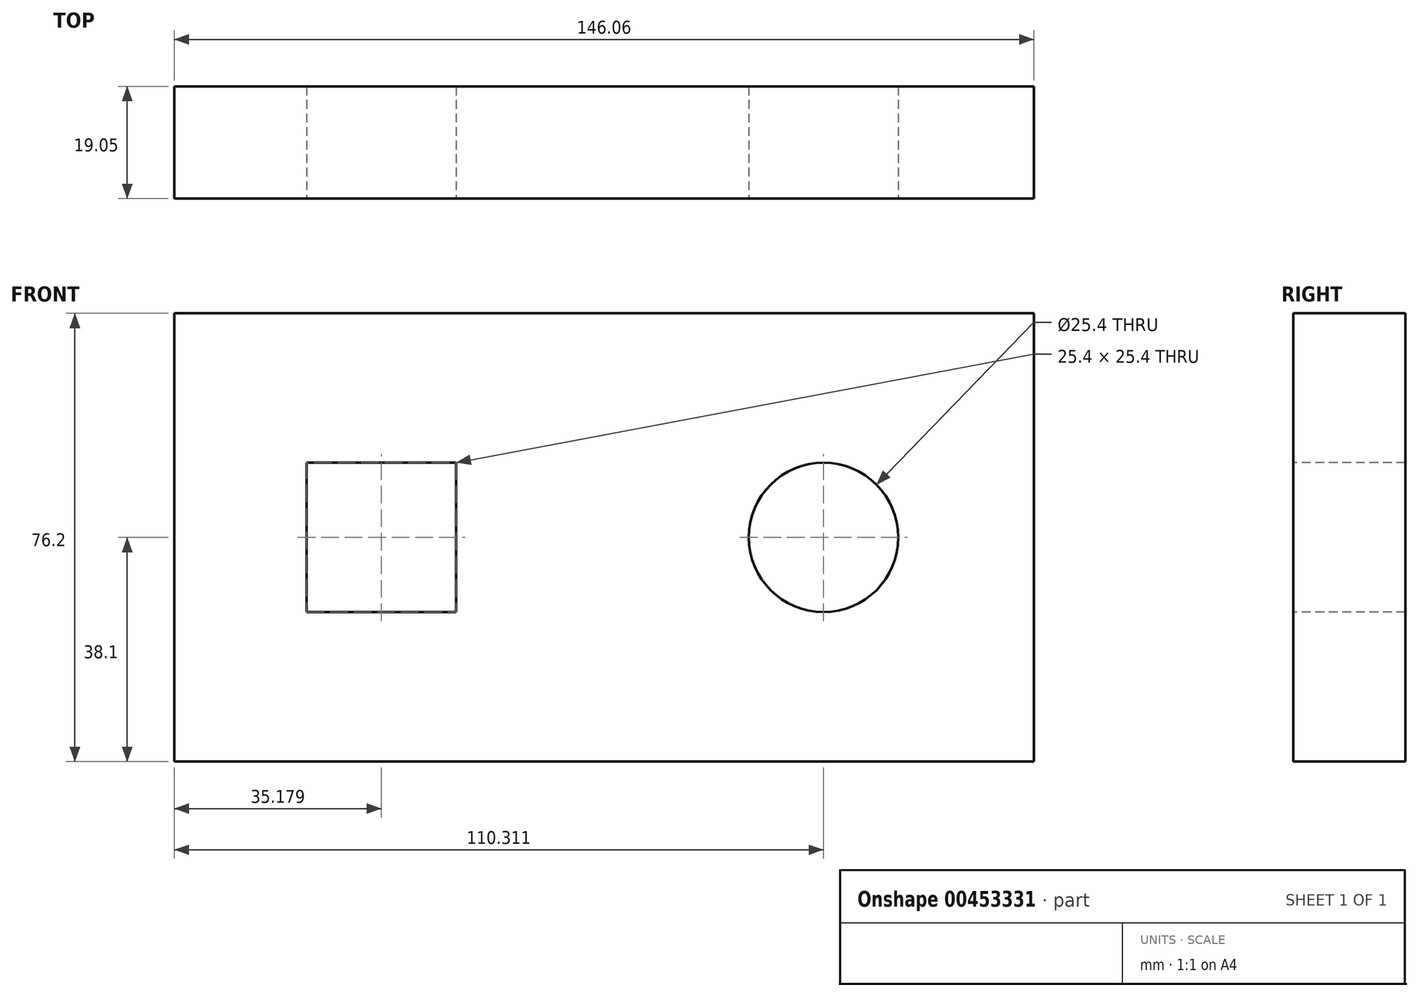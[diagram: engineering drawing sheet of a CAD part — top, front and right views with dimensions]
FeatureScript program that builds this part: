
annotation { "Feature Type Name" : "Feature", "Feature Type Description" : "" }
export const myFeature = defineFeature(function(context is Context, id is Id, definition is map)
    precondition{}
    {
        {
            var Q0;
            Q0=qCreatedBy(makeId("Front.planeOp"),FACE);
            var sketch = newSketch(context, id + "F0", { "sketchPlane" : qUnion([Q0])});
            skLineSegment(sketch, "E0.bottom", {"start": v(73.03, 38.1) * mm, "end": v(-73.03, 38.1) * mm});
            skLineSegment(sketch, "E0.top", {"start": v(73.03, -38.1) * mm, "end": v(-73.03, -38.1) * mm});
            skLineSegment(sketch, "E0.left", {"start": v(73.03, 38.1) * mm, "end": v(73.03, -38.1) * mm});
            skLineSegment(sketch, "E0.right", {"start": v(-73.03, 38.1) * mm, "end": v(-73.03, -38.1) * mm});
            skPoint(sketch, "E0.middle", {"position": v(0, 0) * mm});
            skSolve(sketch);
        }
        {
            var Q0;
            Q0 = qSketchRegion(id + "F0", true);
            extrude(context, id + "F1", {"entities" : qUnion([Q0]), "depth" : 19.05 * mm});
        }
        {
            var Q0;
            Q0=makeQuery(id+"F1.opExtrude","CAP_FACE",FACE,{"disambiguationData":[OSD([sQuery(id+"F0.wireOp",EDGE,"E0.bottom"),sQuery(id+"F0.wireOp",EDGE,"E0.top"),sQuery(id+"F0.wireOp",EDGE,"E0.left"),sQuery(id+"F0.wireOp",EDGE,"E0.right")])],"isStart":false});
            var sketch = newSketch(context, id + "F2", { "sketchPlane" : qUnion([Q0])});
            skLineSegment(sketch, "E1.bottom", {"start": v(-25.15, -12.7) * mm, "end": v(-50.55, -12.7) * mm});
            skLineSegment(sketch, "E1.top", {"start": v(-25.15, 12.7) * mm, "end": v(-50.55, 12.7) * mm});
            skLineSegment(sketch, "E1.left", {"start": v(-25.15, -12.7) * mm, "end": v(-25.15, 12.7) * mm});
            skLineSegment(sketch, "E1.right", {"start": v(-50.55, -12.7) * mm, "end": v(-50.55, 12.7) * mm});
            skPoint(sketch, "E1.middle", {"position": v(-37.85, 0) * mm});
            skPoint(sketch, "E1.middle.positionSnap0", {"position": v(-73.03, 0) * mm});
            skPoint(sketch, "E1.centerSnap0", {"position": v(-73.03, 0) * mm});
            skSolve(sketch);
        }
        {
            var Q0;
            Q0 = qSketchRegion(id + "F2", true);
            extrude(context, id + "F3", {"entities" : qUnion([Q0]), "operationType" : NewBodyOperationType.REMOVE, "oppositeDirection" : true, "depth" : 19.05 * mm});
        }
        {
            var Q0;
            Q0=makeQuery(id+"F1.opExtrude","CAP_FACE",FACE,{"disambiguationData":[OSD([sQuery(id+"F0.wireOp",EDGE,"E0.bottom"),sQuery(id+"F0.wireOp",EDGE,"E0.top"),sQuery(id+"F0.wireOp",EDGE,"E0.left"),sQuery(id+"F0.wireOp",EDGE,"E0.right")])],"isStart":false});
            var sketch = newSketch(context, id + "F4", { "sketchPlane" : qUnion([Q0])});
            skCircle(sketch, "E2", {"center": v(37.28, 0) * mm, "radius": 12.7 * mm});
            skSolve(sketch);
        }
        {
            var Q0;
            Q0 = qSketchRegion(id + "F4", true);
            extrude(context, id + "F5", {"entities" : qUnion([Q0]), "operationType" : NewBodyOperationType.REMOVE, "oppositeDirection" : true, "depth" : 19.05 * mm});
        }
    });
